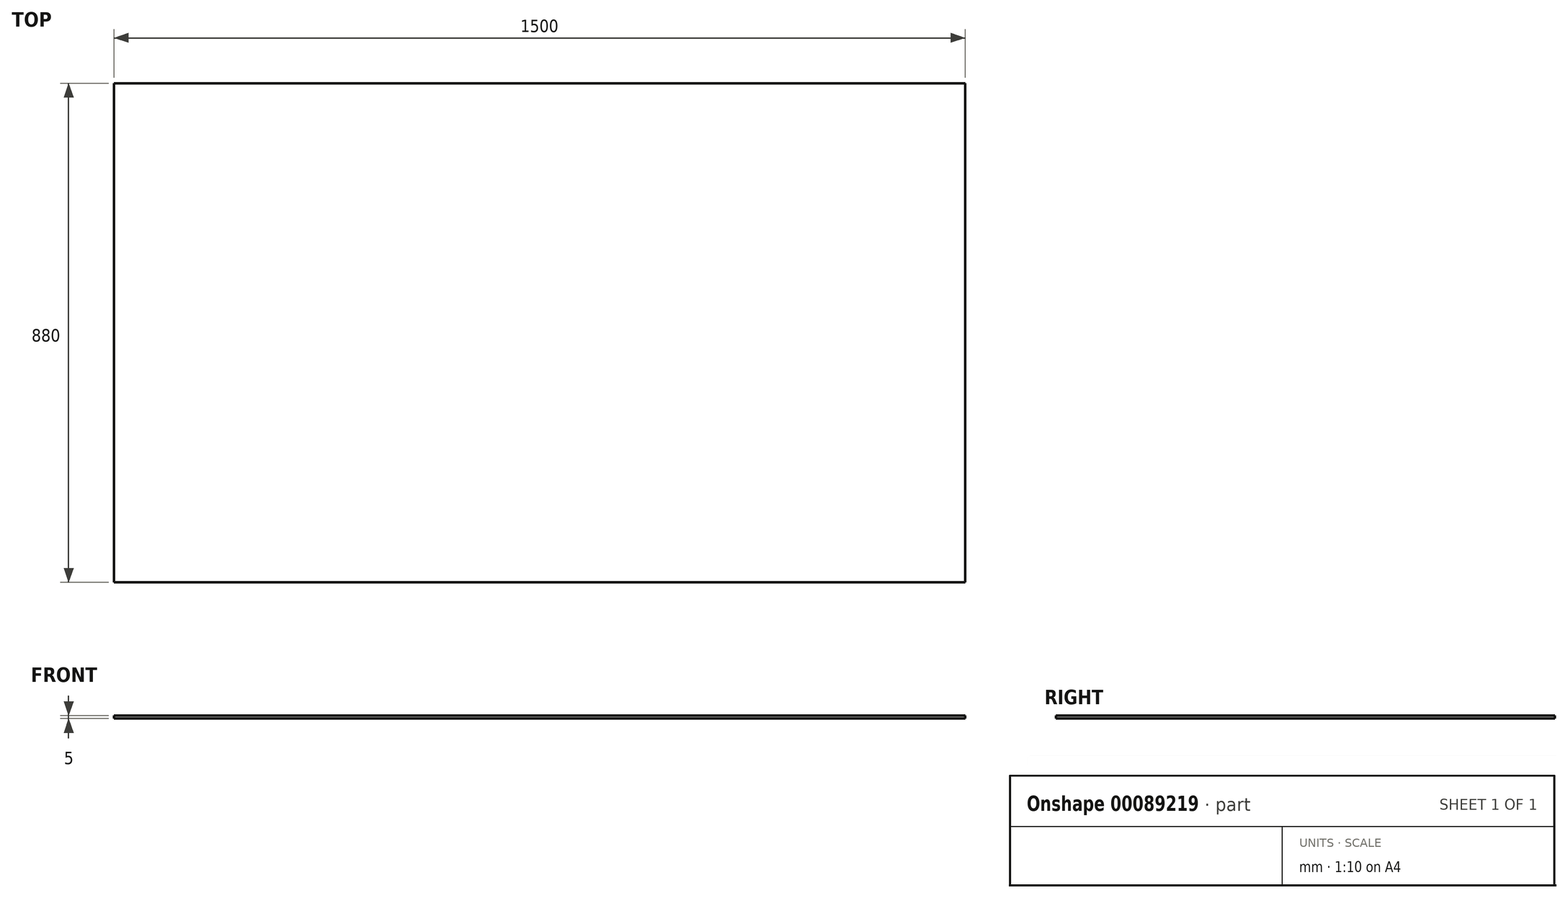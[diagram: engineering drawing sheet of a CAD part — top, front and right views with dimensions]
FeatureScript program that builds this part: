
annotation { "Feature Type Name" : "Feature", "Feature Type Description" : "" }
export const myFeature = defineFeature(function(context is Context, id is Id, definition is map)
    precondition{}
    {
        {
            var Q0;
            Q0=qCreatedBy(makeId("Top.planeOp"),FACE);
            var sketch = newSketch(context, id + "F0", { "sketchPlane" : qUnion([Q0])});
            skLineSegment(sketch, "E0.bottom", {"start": v(750, 440) * mm, "end": v(-750, 440) * mm});
            skLineSegment(sketch, "E0.top", {"start": v(750, -440) * mm, "end": v(-750, -440) * mm});
            skLineSegment(sketch, "E0.left", {"start": v(750, 440) * mm, "end": v(750, -440) * mm});
            skLineSegment(sketch, "E0.right", {"start": v(-750, 440) * mm, "end": v(-750, -440) * mm});
            skPoint(sketch, "E0.middle", {"position": v(0, 0) * mm});
            skSolve(sketch);
        }
        {
            var Q0;
            Q0=makeQuery(id+"F0.imprint","IMPRINT",FACE,{"disambiguationData":[TD([[makeQuery(id+"F0.imprint","IMPRINT",EDGE,{"derivedFrom":sQuery(id+"F0.wireOp",EDGE,"E0.bottom")}),1.0]])]});
            extrude(context, id + "F1", {"entities" : qUnion([Q0]), "depth" : 5 * mm});
        }
    });
